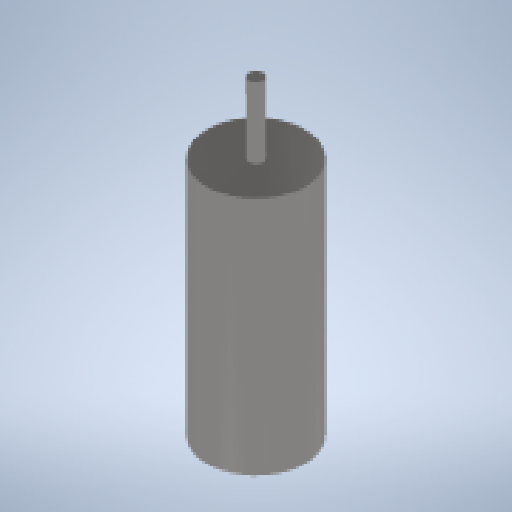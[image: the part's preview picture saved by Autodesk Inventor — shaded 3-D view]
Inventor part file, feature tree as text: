
AUTODESK INVENTOR PART (.ipt)
format: ipt  version: 2023.1 (Build 271208000, 208)  size: 149,504 bytes
history: native  units: mm
features: extrude x3, sketch x3
ambient origin geometry x8: Origin, YZ Plane, XZ Plane, XY Plane, X Axis, Y Axis, Z Axis, Center Point
bodies: Solid1 (feature_tree)
feature tree (6):
  extrude  "Extrusion1"  Depth=17.0mm TaperAngle=0.0deg
  extrude  "Extrusion2"  Depth=5.0mm TaperAngle=0.0deg
  extrude  "Extrusion3"  Depth=0.1mm
  sketch  "Sketch1"  dims[d0=7.0mm d1=17.0mm d2=0.0mm]
  sketch  "Sketch2"  dims[d3=1.0mm d4=5.0mm d5=0.0mm]
  sketch  "Sketch3"  dims[d6=0.1mm d7=0.0mm d8=0.49mm d9=0.49mm]
